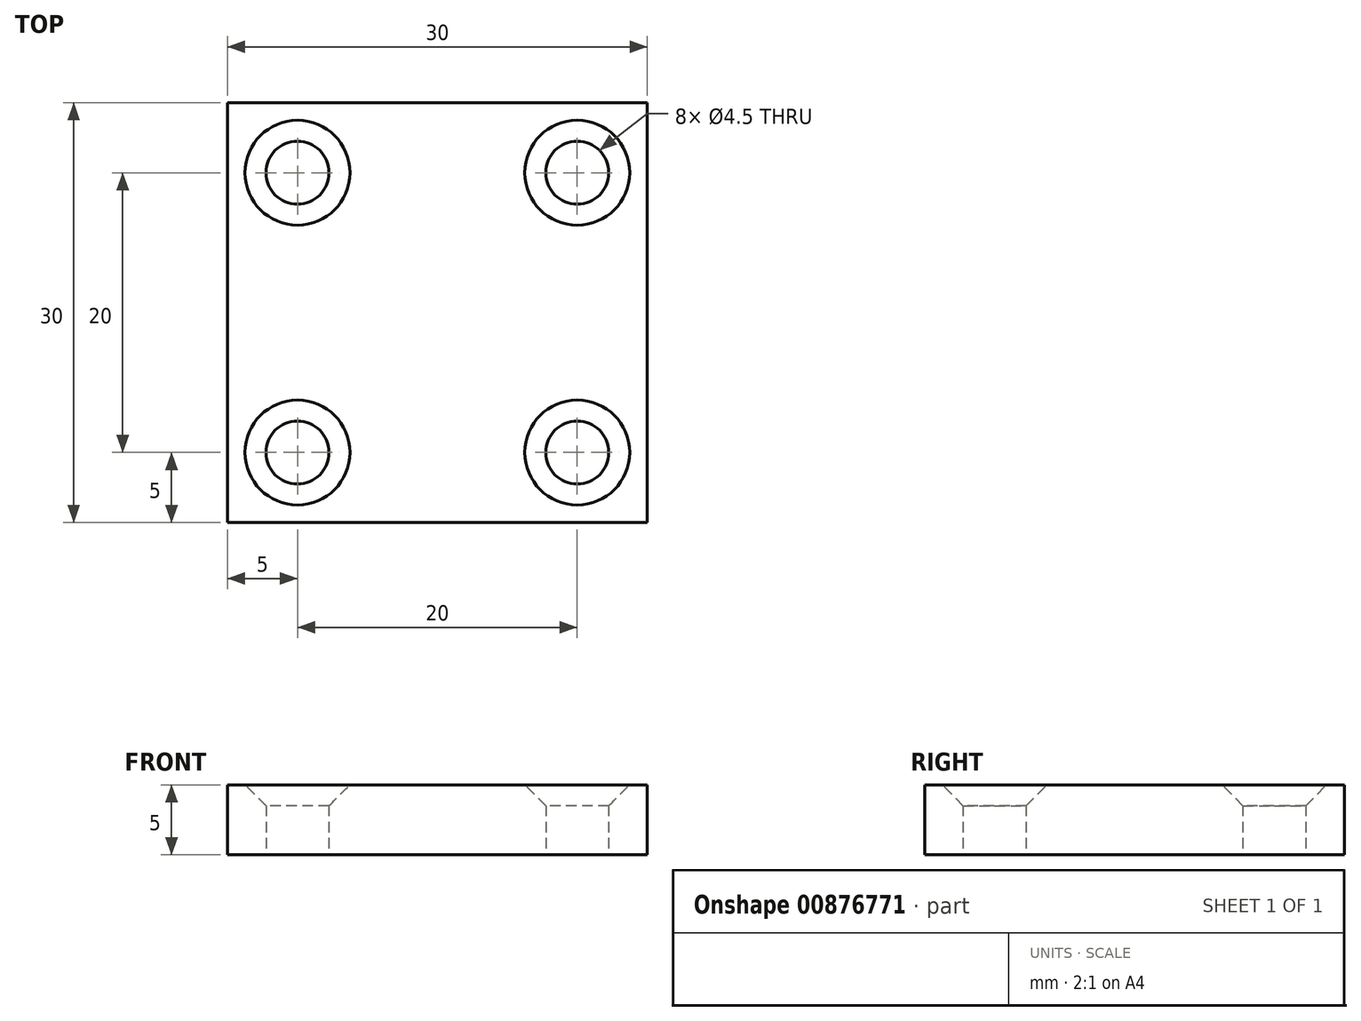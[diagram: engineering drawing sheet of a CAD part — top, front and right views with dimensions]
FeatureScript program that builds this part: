
annotation { "Feature Type Name" : "Feature", "Feature Type Description" : "" }
export const myFeature = defineFeature(function(context is Context, id is Id, definition is map)
    precondition{}
    {
        {
            var Q0;
            Q0=qCreatedBy(makeId("Top.planeOp"),FACE);
            var sketch = newSketch(context, id + "F0", { "sketchPlane" : qUnion([Q0])});
            skLineSegment(sketch, "E0.bottom", {"start": v(-15, 15) * mm, "end": v(15, 15) * mm});
            skLineSegment(sketch, "E0.top", {"start": v(-15, -15) * mm, "end": v(15, -15) * mm});
            skLineSegment(sketch, "E0.left", {"start": v(-15, 15) * mm, "end": v(-15, -15) * mm});
            skLineSegment(sketch, "E0.right", {"start": v(15, 15) * mm, "end": v(15, -15) * mm});
            skPoint(sketch, "E0.middle", {"position": v(0, 0) * mm});
            skCircle(sketch, "E1", {"center": v(-10, 10) * mm, "radius": 2.25 * mm});
            skCircle(sketch, "E2", {"center": v(-10, -10) * mm, "radius": 2.25 * mm});
            skCircle(sketch, "E3", {"center": v(10, -10) * mm, "radius": 2.25 * mm});
            skCircle(sketch, "E4", {"center": v(10, 10) * mm, "radius": 2.25 * mm});
            skSolve(sketch);
        }
        {
            var Q0;
            Q0=makeQuery(id+"F0.imprint","IMPRINT",FACE,{"disambiguationData":[TD([[makeQuery(id+"F0.imprint","IMPRINT",EDGE,{"derivedFrom":sQuery(id+"F0.wireOp",EDGE,"E0.bottom")}),-1.0]])]});
            extrude(context, id + "F1", {"entities" : qUnion([Q0]), "depth" : 5 * mm, "offsetDistance" : 25 * mm});
        }
        {
            var Q0;
            Q0=makeQuery(id+"F1.opExtrude","CAP_EDGE",EDGE,{"disambiguationData":[OSD([sQuery(id+"F0.wireOp",EDGE,"E2")])],"isStart":false});
            var Q1;
            Q1=makeQuery(id+"F1.opExtrude","CAP_EDGE",EDGE,{"disambiguationData":[OSD([sQuery(id+"F0.wireOp",EDGE,"E1")])],"isStart":false});
            var Q2;
            Q2=makeQuery(id+"F1.opExtrude","CAP_EDGE",EDGE,{"disambiguationData":[OSD([sQuery(id+"F0.wireOp",EDGE,"E3")])],"isStart":false});
            var Q3;
            Q3=makeQuery(id+"F1.opExtrude","CAP_EDGE",EDGE,{"disambiguationData":[OSD([sQuery(id+"F0.wireOp",EDGE,"E4")])],"isStart":false});
            chamfer(context, id + "F2", {"entities" : qUnion([Q0, Q1, Q2, Q3]), "width" : 1.5 * mm, "tangentPropagation" : true});
        }
    });
